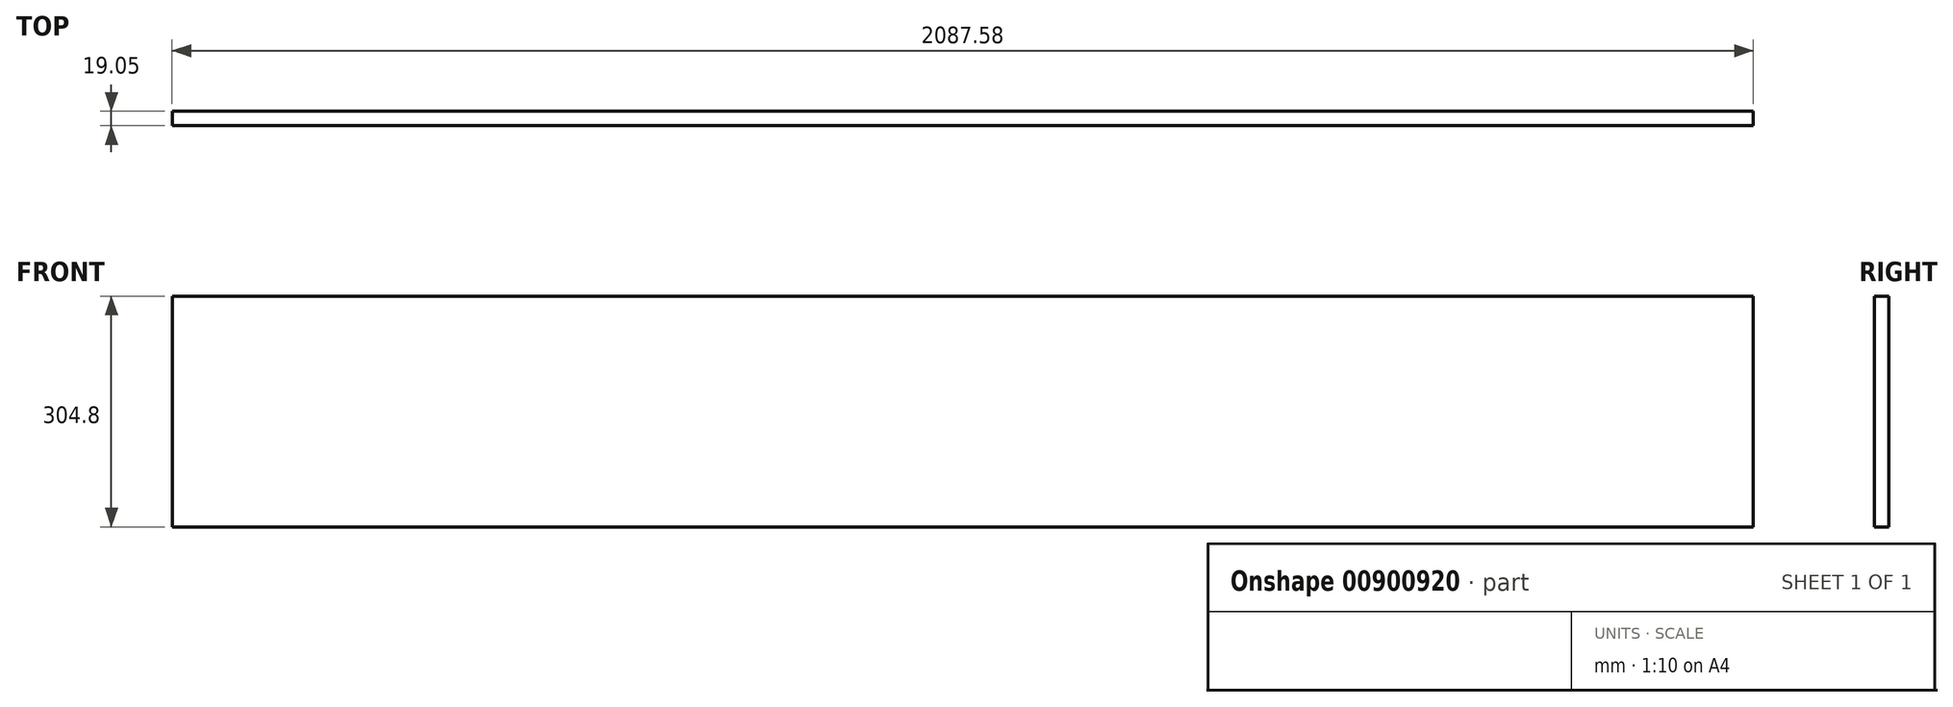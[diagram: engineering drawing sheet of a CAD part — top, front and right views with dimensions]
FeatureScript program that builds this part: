
annotation { "Feature Type Name" : "Feature", "Feature Type Description" : "" }
export const myFeature = defineFeature(function(context is Context, id is Id, definition is map)
    precondition{}
    {
        {
            var Q0;
            Q0=qCreatedBy(makeId("Front.planeOp"),FACE);
            var sketch = newSketch(context, id + "F0", { "sketchPlane" : qUnion([Q0])});
            skLineSegment(sketch, "E0.bottom", {"start": v(-1043.79, 152.4) * mm, "end": v(1043.79, 152.4) * mm});
            skLineSegment(sketch, "E0.top", {"start": v(-1043.79, -152.4) * mm, "end": v(1043.79, -152.4) * mm});
            skLineSegment(sketch, "E0.left", {"start": v(-1043.79, 152.4) * mm, "end": v(-1043.79, -152.4) * mm});
            skLineSegment(sketch, "E0.right", {"start": v(1043.79, 152.4) * mm, "end": v(1043.79, -152.4) * mm});
            skPoint(sketch, "E0.middle", {"position": v(0, 0) * mm});
            skSolve(sketch);
        }
        {
            var Q0;
            Q0=makeQuery(id+"F0.imprint","IMPRINT",FACE,{"disambiguationData":[TD([[makeQuery(id+"F0.imprint","IMPRINT",EDGE,{"derivedFrom":sQuery(id+"F0.wireOp",EDGE,"E0.bottom")}),-1.0]])]});
            extrude(context, id + "F1", {"entities" : qUnion([Q0]), "depth" : 19.05 * mm, "offsetDistance" : 25.4 * mm});
        }
    });
